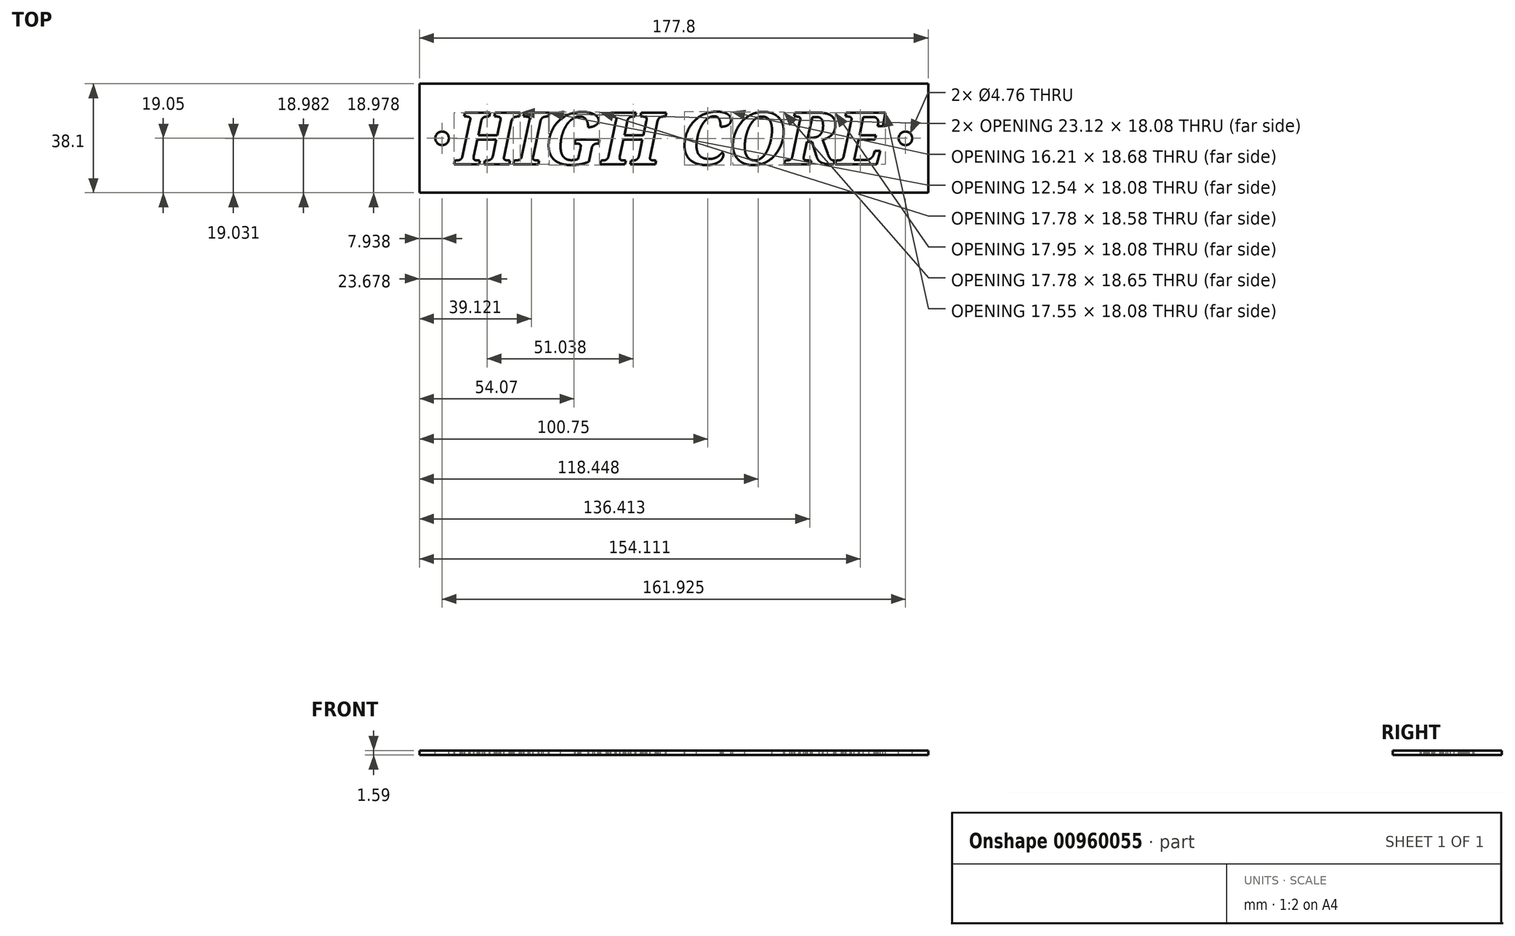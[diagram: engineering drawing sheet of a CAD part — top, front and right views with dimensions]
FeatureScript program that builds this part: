
annotation { "Feature Type Name" : "Feature", "Feature Type Description" : "" }
export const myFeature = defineFeature(function(context is Context, id is Id, definition is map)
    precondition{}
    {
        {
            var Q0;
            Q0=qCreatedBy(makeId("Top.planeOp"),FACE);
            var sketch = newSketch(context, id + "F0", { "sketchPlane" : qUnion([Q0])});
            skLineSegment(sketch, "E0.bottom", {"start": v(88.9, -19.05) * mm, "end": v(-88.9, -19.05) * mm});
            skLineSegment(sketch, "E0.top", {"start": v(88.9, 19.05) * mm, "end": v(-88.9, 19.05) * mm});
            skLineSegment(sketch, "E0.left", {"start": v(88.9, -19.05) * mm, "end": v(88.9, 19.05) * mm});
            skLineSegment(sketch, "E0.right", {"start": v(-88.9, -19.05) * mm, "end": v(-88.9, 19.05) * mm});
            skPoint(sketch, "E0.middle", {"position": v(0, 0) * mm});
            skSolve(sketch);
        }
        {
            var Q0;
            Q0=makeQuery(id+"F0.imprint","IMPRINT",FACE,{"disambiguationData":[TD([[makeQuery(id+"F0.imprint","IMPRINT",EDGE,{"derivedFrom":sQuery(id+"F0.wireOp",EDGE,"E0.bottom")}),-1.0]])]});
            extrude(context, id + "F1", {"entities" : qUnion([Q0]), "depth" : 1.59 * mm, "offsetDistance" : 25.4 * mm});
        }
        {
            var Q0;
            Q0=makeQuery(id+"F1.opExtrude","CAP_FACE",FACE,{"disambiguationData":[OSD([sQuery(id+"F0.wireOp",EDGE,"E0.bottom"),sQuery(id+"F0.wireOp",EDGE,"E0.top"),sQuery(id+"F0.wireOp",EDGE,"E0.left"),sQuery(id+"F0.wireOp",EDGE,"E0.right")])],"isStart":false});
            var sketch = newSketch(context, id + "F2", { "sketchPlane" : qUnion([Q0])});
            skText(sketch, "E1", { "text": "HIGH CORE", "fontName": "NotoSerif-BoldItalic.ttf"});
            skPoint(sketch, "E2", {"position": v(0, 0) * mm});
            skCircle(sketch, "E3", {"center": v(-80.96, 0) * mm, "radius": 2.38 * mm});
            skCircle(sketch, "E4", {"center": v(80.96, 0) * mm, "radius": 2.38 * mm});
            skLineSegment(sketch, "E5", {"start": v(-80.96, 0) * mm, "end": v(0, 0) * mm, "construction": true});
            skLineSegment(sketch, "E6", {"start": v(0, 0) * mm, "end": v(80.96, 0) * mm, "construction": true});
            const initialGuessF2  = {"E1": [-0.0762, -0.00911, 1, 0, 0.01823]};
            skSetInitialGuess(sketch, initialGuessF2);
            skSolve(sketch);
        }
        {
            var Q0;
            Q0=qSketchRegion(id+"F2",true);
            extrude(context, id + "F3", {"entities" : qUnion([Q0]), "operationType" : NewBodyOperationType.REMOVE, "oppositeDirection" : true, "depth" : 25.4 * mm, "offsetDistance" : 25.4 * mm});
        }
    });
